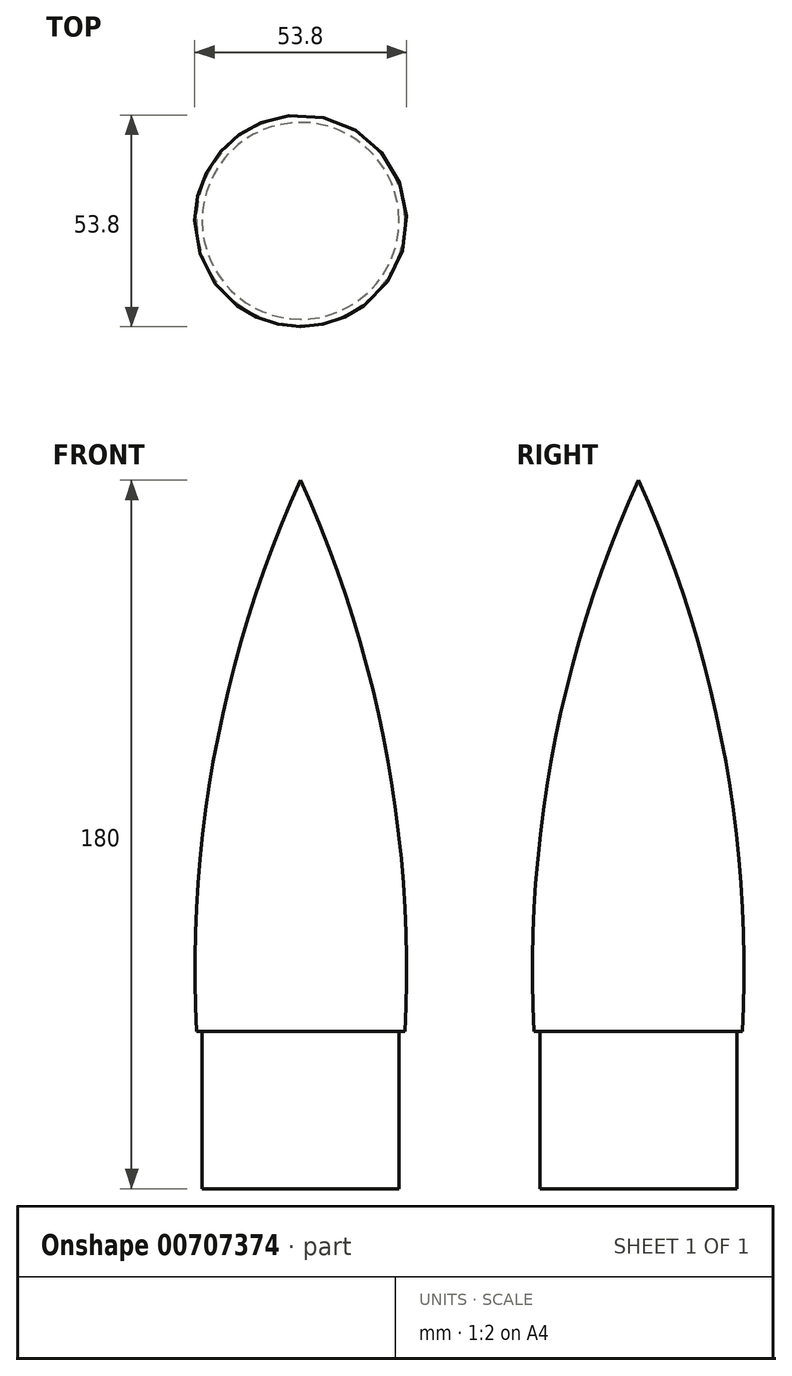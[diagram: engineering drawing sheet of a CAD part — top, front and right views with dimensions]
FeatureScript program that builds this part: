
annotation { "Feature Type Name" : "Feature", "Feature Type Description" : "" }
export const myFeature = defineFeature(function(context is Context, id is Id, definition is map)
    precondition{}
    {
        {
            var Q0;
            Q0=qCreatedBy(makeId("Front.planeOp"),FACE);
            var sketch = newSketch(context, id + "F0", { "sketchPlane" : qUnion([Q0])});
            skLineSegment(sketch, "E0", {"start": v(0, -40) * mm, "end": v(25, -40) * mm});
            skLineSegment(sketch, "E1", {"start": v(25, -40) * mm, "end": v(25, 0) * mm});
            skLineSegment(sketch, "E2", {"start": v(25, 0) * mm, "end": v(26.5, 0) * mm});
            skArc(sketch, "E3", {"start": v(26.5, 0) * mm, "mid": v(21.63, 71.59) * mm, "end": v(0, 140) * mm});
            skLineSegment(sketch, "E4", {"start": v(0, 140) * mm, "end": v(0, -40) * mm});
            skSolve(sketch);
        }
        {
            var Q0;
            Q0=makeQuery(id+"F0.imprint","IMPRINT",FACE,{"disambiguationData":[TD([[makeQuery(id+"F0.imprint","IMPRINT",EDGE,{"derivedFrom":sQuery(id+"F0.wireOp",EDGE,"E0")}),1.0]])]});
            var Q1;
            Q1=sQuery(id+"F0.wireOp",EDGE,"E4");
            revolve(context, id + "F1", {"surfaceOperationType" : NewSurfaceOperationType.NEW, "entities" : qUnion([Q0]), "axis" : qUnion([Q1]), "revolveType" : RevolveType.FULL});
        }
    });
